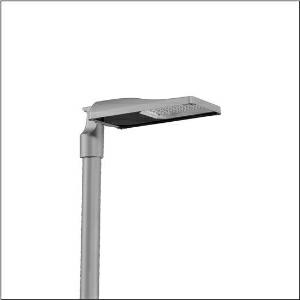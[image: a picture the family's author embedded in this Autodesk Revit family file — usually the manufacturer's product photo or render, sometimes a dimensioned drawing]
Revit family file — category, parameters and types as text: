
# Revit family: streetlight_sl_31_mini___st1_0a_5xh6d3aa08ha_c65b
name_source: partatom
category: Lighting Fixtures
units: mm (PartAtom-declared; Revit-internal decimal feet)

## family parameters
Cut with Voids When Loaded = No
Host = Face
Light Source = No
Part Type = Normal
Room Calculation Point = No
Round Connector Dimension = Use Diameter
Shared = No

## types (1)
- --- (1 x LED, 9240 lm, 68.3 W, 3000K)
    Apparent Load = 68 VA
    CIE Flux Codes = 37 72 97 100 100
    Color Rendering = 70
    Color Temperature = 3000K
    Default Elevation = 1800 mm
    Description = Streetlight SL 31 mini Easy mast luminaire for post-top, side-entry; light control with lens of PMMA; light distribution: ST1.0a, direct asymmetric distribution, for standard-compliant lighting for roads and squares; LED: luminous flux: 9.240lm, light colour: 730, colour temperature: 3000K; luminous efficacy: 135,3lm/W; control: pre-setting: linear dimming characteristic, flexible luminous flux parameterisation, time-dependent luminous flux control, constant luminous flux control, intelligent temperature release in ECG and LED module, overheat protection; luminaire housing, of diecast aluminium, Siteco® metallic grey (DB 702S), corrosivity category C5 high according to DIN EN ISO 12944; cover of toughened safety glass, transparent, opened without tools; mast flange of diecast aluminium, Siteco® metallic grey (DB 702S), spigot size: 76/60mm, mast flange included unmounted; with cable H07RN-F 2x 1.5mm², cable length: 8,5m, connection cable pre-assembled; mains connection: 220..240V, AC, 50/60Hz; power consumption (at start of service life): 68,3W / (at end of service life): 74,8W / (with reduced operation 50%): 29,7W; protection rating (complete): IP66; insulation class (complete): insulation class II (safety insulation); impact resistance: IK10; certification: CE, ENEC, ENEC+, VDE, UKCA; permissible operating ambient temperature for outdoor applications: -40..+50°C; packaging unit: 1 piece

Light Distribution: ST1.0a
    Height = 76 mm
    Lamp = 1 x LED
    Lamp Light Flux = 9240 lm
    Lamp Power = 68.3 W
    Lamp count = 1
    Length = 547 mm
    Luminous efficacy = 135 lm/W
    Manufacturer = Siteco
    ModVariant = No
    Model = 5XH6D3AA08HA
    Number of Poles = 1
    OnlyDefault = Yes
    Power Factor = 1
    Product Name = Streetlight SL 31 mini | ST1.0a
    Product group = mast luminaire | pylon top
    ProductGroupID = 6100
    Protection Class = Protection class II
    Protection Degree = IP 66
    RLX_Detail_Level = 1
    RLX_Emergency_Light_Flux = 0 lm
    RLX_Emergency_Type = 0
    RLX_Emergency_Type_DB = No
    RlxData = <blob elided: 39469 chars, md5=4d6db56e>
    Socket = socket
    Standby Power = 0 W
    System Light Flux = 9240 lm
    System Power = 68 W
    Type Comments = factory setting: luminous flux: 100 % | dim-lin: 254 | 693 mA
    Type Image = l_1300326.jpg
    URL = http://relux.com
    VarID = @adj_054272
    Voltage = 0 V
    Weight = 0.00 kg
    Width = 265 mm

## geometry (parser evidence)
native form markers: Blend x4, Sweep x9
no freeform markers — native parametric forms only
